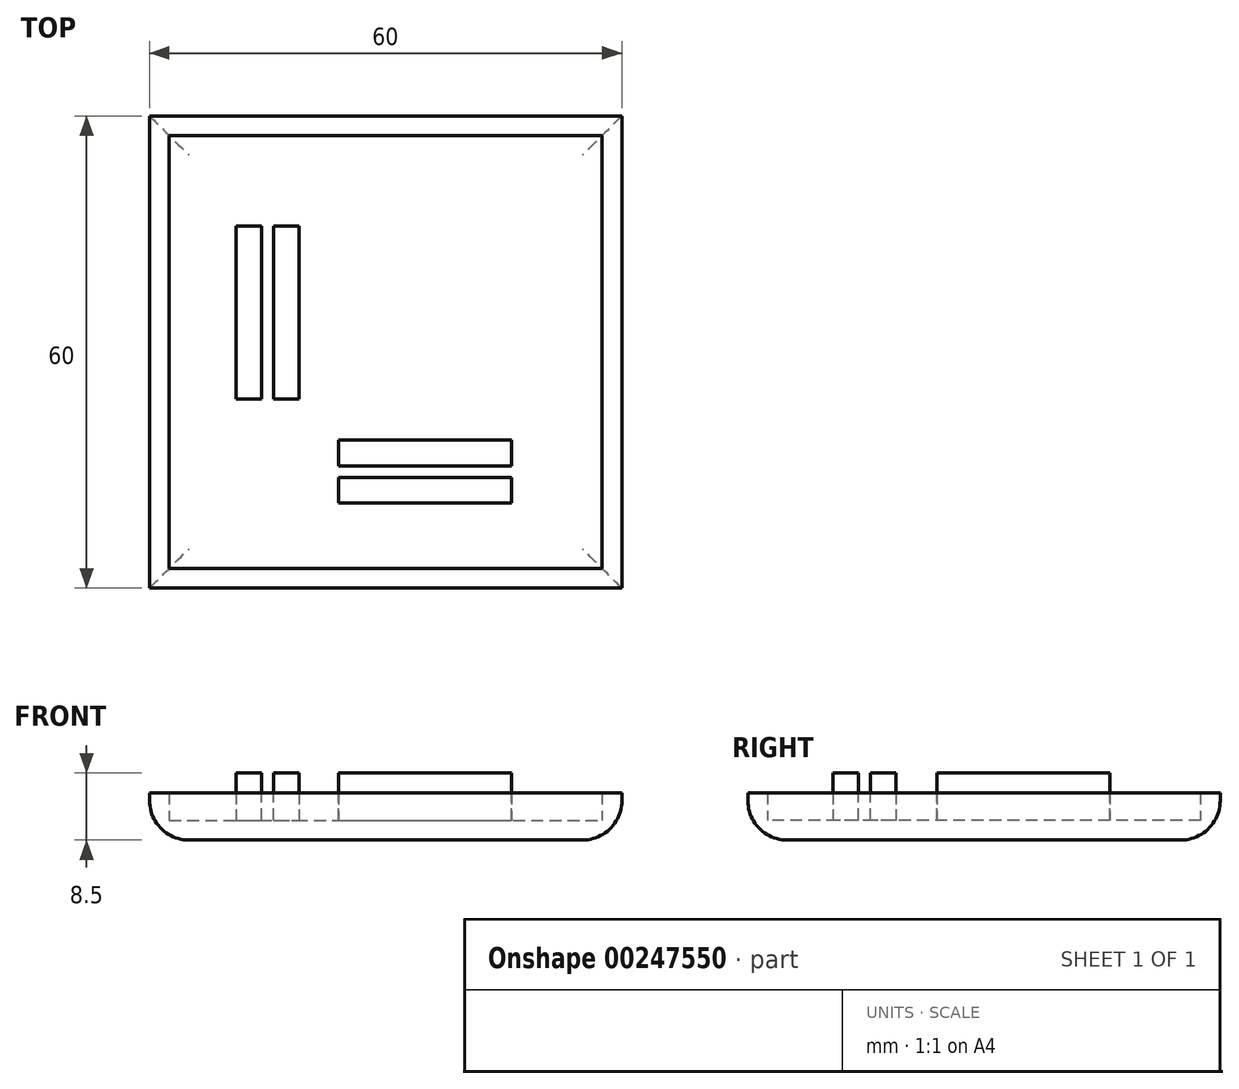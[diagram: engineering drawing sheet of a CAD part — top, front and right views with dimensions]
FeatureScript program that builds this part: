
annotation { "Feature Type Name" : "Feature", "Feature Type Description" : "" }
export const myFeature = defineFeature(function(context is Context, id is Id, definition is map)
    precondition{}
    {
        {
            var Q0;
            Q0=qCreatedBy(makeId("Top.planeOp"),FACE);
            var sketch = newSketch(context, id + "F0", { "sketchPlane" : qUnion([Q0])});
            skLineSegment(sketch, "E0.bottom", {"start": v(0, 0) * mm, "end": v(60, 0) * mm});
            skLineSegment(sketch, "E0.top", {"start": v(0, -60) * mm, "end": v(60, -60) * mm});
            skLineSegment(sketch, "E0.left", {"start": v(0, 0) * mm, "end": v(0, -60) * mm});
            skLineSegment(sketch, "E0.right", {"start": v(60, 0) * mm, "end": v(60, -60) * mm});
            skSolve(sketch);
        }
        {
            var Q0;
            Q0 = qSketchRegion(id + "F0", true);
            extrude(context, id + "F1", {"entities" : qUnion([Q0]), "depth" : 6 * mm});
        }
        {
            var Q0;
            Q0=makeQuery(id+"F1.opExtrude","CAP_FACE",FACE,{"disambiguationData":[OSD([sQuery(id+"F0.wireOp",EDGE,"E0.bottom"),sQuery(id+"F0.wireOp",EDGE,"E0.top"),sQuery(id+"F0.wireOp",EDGE,"E0.left"),sQuery(id+"F0.wireOp",EDGE,"E0.right")])],"isStart":false});
            shell(context, id + "F2", {"entities" : qUnion([Q0]), "thickness" : 2.5 * mm});
        }
        {
            var Q0;
            Q0=makeQuery(id+"F2.opShell","OFFSET_FACE",FACE,{"disambiguationData":[OSD([sQuery(id+"F0.wireOp",EDGE,"E0.bottom"),sQuery(id+"F0.wireOp",EDGE,"E0.top"),sQuery(id+"F0.wireOp",EDGE,"E0.left"),sQuery(id+"F0.wireOp",EDGE,"E0.right")])]});
            var sketch = newSketch(context, id + "F3", { "sketchPlane" : qUnion([Q0])});
            skLineSegment(sketch, "E1", {"start": v(11, -14) * mm, "end": v(11, -36) * mm});
            skLineSegment(sketch, "E2", {"start": v(11, -36) * mm, "end": v(19, -36) * mm});
            skLineSegment(sketch, "E3", {"start": v(19, -36) * mm, "end": v(19, -14) * mm});
            skLineSegment(sketch, "E4", {"start": v(46, -41.2) * mm, "end": v(24, -41.2) * mm});
            skLineSegment(sketch, "E5", {"start": v(24, -41.2) * mm, "end": v(24, -49.2) * mm});
            skLineSegment(sketch, "E6", {"start": v(24, -49.2) * mm, "end": v(46, -49.2) * mm});
            skLineSegment(sketch, "E7", {"start": v(11, -14) * mm, "end": v(19, -14) * mm});
            skLineSegment(sketch, "E8", {"start": v(46, -41.2) * mm, "end": v(46, -49.2) * mm});
            skSolve(sketch);
        }
        {
            var Q0;
            Q0 = qSketchRegion(id + "F3", true);
            extrude(context, id + "F4", {"entities" : qUnion([Q0]), "operationType" : NewBodyOperationType.ADD, "depth" : 6 * mm});
        }
        {
            var Q0;
            Q0=makeQuery(id+"F4.opExtrude","CAP_FACE",FACE,{"disambiguationData":[OSD([sQuery(id+"F3.wireOp",EDGE,"E1"),sQuery(id+"F3.wireOp",EDGE,"E2"),sQuery(id+"F3.wireOp",EDGE,"E3"),sQuery(id+"F3.wireOp",EDGE,"E7")])],"isStart":false});
            var sketch = newSketch(context, id + "F5", { "sketchPlane" : qUnion([Q0])});
            skLineSegment(sketch, "E9.bottom", {"start": v(14.25, -14) * mm, "end": v(15.75, -14) * mm});
            skLineSegment(sketch, "E9.top", {"start": v(14.25, -36) * mm, "end": v(15.75, -36) * mm});
            skLineSegment(sketch, "E9.left", {"start": v(14.25, -14) * mm, "end": v(14.25, -36) * mm});
            skLineSegment(sketch, "E9.right", {"start": v(15.75, -14) * mm, "end": v(15.75, -36) * mm});
            skSolve(sketch);
        }
        {
            var Q0;
            Q0=makeQuery(id+"F4.opExtrude","CAP_FACE",FACE,{"disambiguationData":[OSD([sQuery(id+"F3.wireOp",EDGE,"E4"),sQuery(id+"F3.wireOp",EDGE,"E5"),sQuery(id+"F3.wireOp",EDGE,"E6"),sQuery(id+"F3.wireOp",EDGE,"E8")])],"isStart":false});
            var sketch = newSketch(context, id + "F6", { "sketchPlane" : qUnion([Q0])});
            skLineSegment(sketch, "E10.bottom", {"start": v(24, -44.45) * mm, "end": v(46, -44.45) * mm});
            skLineSegment(sketch, "E10.top", {"start": v(24, -45.95) * mm, "end": v(46, -45.95) * mm});
            skLineSegment(sketch, "E10.left", {"start": v(24, -44.45) * mm, "end": v(24, -45.95) * mm});
            skLineSegment(sketch, "E10.right", {"start": v(46, -44.45) * mm, "end": v(46, -45.95) * mm});
            skSolve(sketch);
        }
        {
            var Q0;
            Q0 = qSketchRegion(id + "F5", true);
            var Q1;
            Q1=makeQuery(id+"F6.imprint","IMPRINT",FACE,{"disambiguationData":[TD([[makeQuery(id+"F6.imprint","IMPRINT",EDGE,{"derivedFrom":sQuery(id+"F6.wireOp",EDGE,"E10.bottom")}),-1.0]])]});
            extrude(context, id + "F7", {"entities" : qUnion([Q0, Q1]), "operationType" : NewBodyOperationType.REMOVE, "oppositeDirection" : true, "depth" : 6 * mm});
        }
        {
            var Q0;
            Q0=makeQuery(id+"F1.opExtrude","CAP_EDGE",EDGE,{"disambiguationData":[OSD([sQuery(id+"F0.wireOp",EDGE,"E0.top")])],"isStart":true});
            var Q1;
            Q1=makeQuery(id+"F1.opExtrude","CAP_EDGE",EDGE,{"disambiguationData":[OSD([sQuery(id+"F0.wireOp",EDGE,"E0.right")])],"isStart":true});
            var Q2;
            Q2=makeQuery(id+"F1.opExtrude","CAP_EDGE",EDGE,{"disambiguationData":[OSD([sQuery(id+"F0.wireOp",EDGE,"E0.left")])],"isStart":true});
            var Q3;
            Q3=makeQuery(id+"F1.opExtrude","CAP_EDGE",EDGE,{"disambiguationData":[OSD([sQuery(id+"F0.wireOp",EDGE,"E0.bottom")])],"isStart":true});
            fillet(context, id + "F8", {"entities" : qUnion([Q0, Q1, Q2, Q3]), "radius" : 5 * mm, "tangentPropagation" : true, "allowEdgeOverflow" : false});
        }
    });
